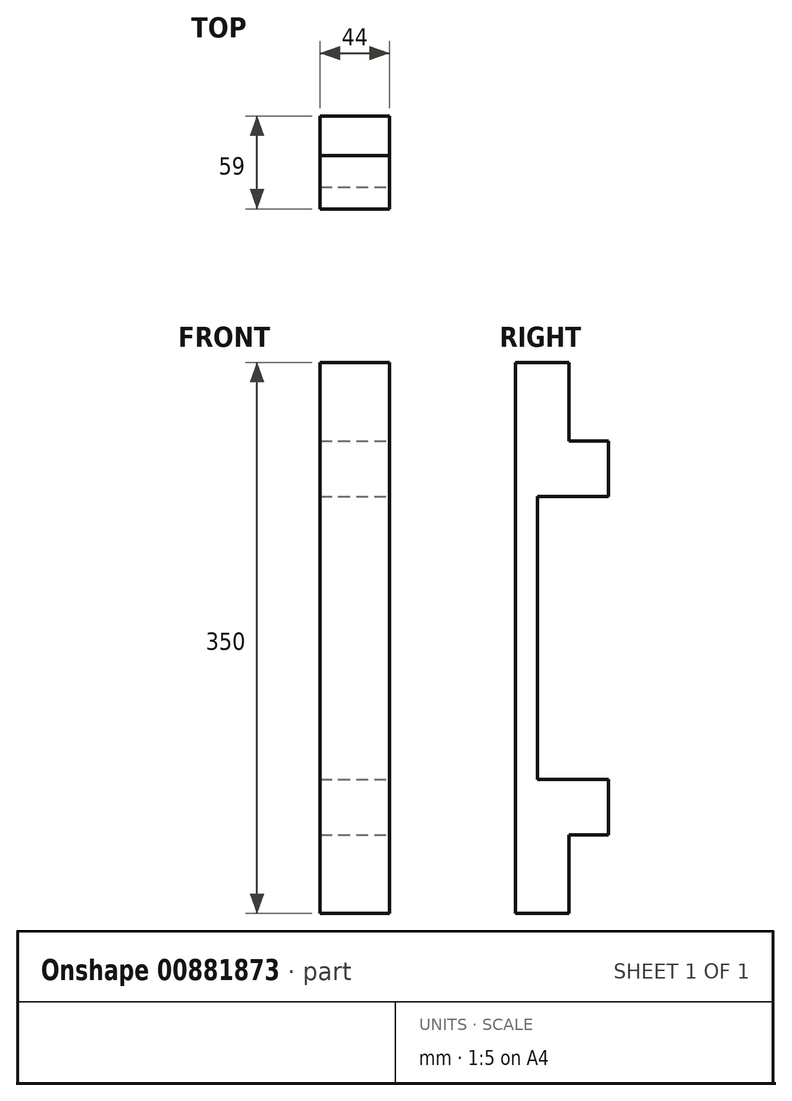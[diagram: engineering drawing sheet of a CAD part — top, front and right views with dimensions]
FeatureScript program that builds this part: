
annotation { "Feature Type Name" : "Feature", "Feature Type Description" : "" }
export const myFeature = defineFeature(function(context is Context, id is Id, definition is map)
    precondition{}
    {
        {
            var Q0;
            Q0=qCreatedBy(makeId("Top.planeOp"),FACE);
            var sketch = newSketch(context, id + "F0", { "sketchPlane" : qUnion([Q0])});
            skLineSegment(sketch, "E0.bottom", {"start": v(22, -34.5) * mm, "end": v(-22, -34.5) * mm});
            skLineSegment(sketch, "E0.top", {"start": v(22, 34.5) * mm, "end": v(-22, 34.5) * mm});
            skLineSegment(sketch, "E0.left", {"start": v(22, -34.5) * mm, "end": v(22, 34.5) * mm});
            skLineSegment(sketch, "E0.right", {"start": v(-22, -34.5) * mm, "end": v(-22, 34.5) * mm});
            skPoint(sketch, "E0.middle", {"position": v(0, 0) * mm});
            skSolve(sketch);
        }
        {
            var Q0;
            Q0=qSketchRegion(id+"F0",true);
            extrude(context, id + "F1", {"entities" : qUnion([Q0]), "depth" : 350 * mm, "offsetDistance" : 25 * mm});
        }
        {
            var Q0;
            Q0=makeQuery(id+"F1.opExtrude","SWEPT_FACE",FACE,{"disambiguationData":[OSD([sQuery(id+"F0.wireOp",EDGE,"E0.left")])]});
            var sketch = newSketch(context, id + "F2", { "sketchPlane" : qUnion([Q0])});
            skLineSegment(sketch, "E1", {"start": v(34.5, 175) * mm, "end": v(-34.5, 175) * mm, "construction": true});
            skLineSegment(sketch, "E2", {"start": v(34.5, 85) * mm, "end": v(-10.5, 85) * mm});
            skLineSegment(sketch, "E3", {"start": v(-10.5, 85) * mm, "end": v(-10.5, 175) * mm});
            skLineSegment(sketch, "E4", {"start": v(34.5, 85) * mm, "end": v(34.5, 175) * mm});
            skLineSegment(sketch, "E5.MirrorCS", {"start": v(34.5, 265) * mm, "end": v(34.5, 175) * mm});
            skLineSegment(sketch, "E6.MirrorCS", {"start": v(34.5, 265) * mm, "end": v(-10.5, 265) * mm});
            skLineSegment(sketch, "E7.MirrorCS", {"start": v(-10.5, 265) * mm, "end": v(-10.5, 175) * mm});
            skLineSegment(sketch, "E8", {"start": v(9.5, 0) * mm, "end": v(9.5, 50) * mm});
            skLineSegment(sketch, "E9", {"start": v(9.5, 50) * mm, "end": v(34.5, 50) * mm});
            skLineSegment(sketch, "E10", {"start": v(9.5, 0) * mm, "end": v(34.5, 0) * mm});
            skLineSegment(sketch, "E11", {"start": v(34.5, 0) * mm, "end": v(34.5, 50) * mm});
            skLineSegment(sketch, "E12.MirrorCS", {"start": v(34.5, 350) * mm, "end": v(34.5, 300) * mm});
            skLineSegment(sketch, "E13.MirrorCS", {"start": v(9.5, 350) * mm, "end": v(34.5, 350) * mm});
            skLineSegment(sketch, "E14.MirrorCS", {"start": v(9.5, 350) * mm, "end": v(9.5, 300) * mm});
            skLineSegment(sketch, "E15.MirrorCS", {"start": v(9.5, 300) * mm, "end": v(34.5, 300) * mm});
            skSolve(sketch);
        }
        {
            var Q0;
            Q0=qSketchRegion(id+"F2",true);
            extrude(context, id + "F3", {"entities" : qUnion([Q0]), "operationType" : NewBodyOperationType.REMOVE, "endBound" : BoundingType.THROUGH_ALL, "oppositeDirection" : true, "depth" : 25 * mm, "offsetDistance" : 25 * mm});
        }
        {
            var Q0;
            Q0=makeQuery(id+"F1.opExtrude","SWEPT_FACE",FACE,{"disambiguationData":[OSD([sQuery(id+"F0.wireOp",EDGE,"E0.left")])]});
            var sketch = newSketch(context, id + "F4", { "sketchPlane" : qUnion([Q0])});
            skLineSegment(sketch, "E16", {"start": v(-24.5, 0) * mm, "end": v(-24.5, 350) * mm});
            skLineSegment(sketch, "E17", {"start": v(-24.5, 350) * mm, "end": v(-34.5, 350) * mm});
            skLineSegment(sketch, "E18", {"start": v(-34.5, 350) * mm, "end": v(-34.5, 0) * mm});
            skLineSegment(sketch, "E19", {"start": v(-34.5, 0) * mm, "end": v(-24.5, 0) * mm});
            skSolve(sketch);
        }
        {
            var Q0;
            Q0 = qSketchRegion(id + "F4", true);
            extrude(context, id + "F5", {"entities" : qUnion([Q0]), "operationType" : NewBodyOperationType.REMOVE, "oppositeDirection" : true, "depth" : 100 * mm, "offsetDistance" : 25 * mm});
        }
    });
